# Revit family: Legrand Cabinet XL³ 400 Insulating
name_source: partatom
category: Equipement électrique
units: mm (PartAtom-declared; Revit-internal decimal feet)

## family parameters
Basée sur le plan de construction = Non
Configuration du panneau = Deux colonnes, circuits au sein
Cote de connecteur circulaire = Utiliser le diamètre
Couper avec des vides une fois chargée = Non
Numéro OmniClass = 23.80.30.11.17
Partagée = Non
Point de calcul de pièce = Non
Titre OmniClass = Distribution Boards and Control Panels
Toujours verticalement = Oui
Type d'élément = Tableau de raccordement

## types (5) — shared parameters
Fabricant = Legrand
Finish = Epoxipolyester paint deposited by electrostatic powder
General Conditions of Use = https://export.legrand.com
ICW (until) (kA) = 25
IK with door = 08
IK without door = 07
IN (A) = 400
IP with door = 40
IP without door = 30
IPK (kA) = 52.5
Material = Steel
Material corner = Plastic
Modèle = XL³ 400 Isolant
RAL = 7035
URL = https://www.legrand.fr
depth (mm) = 175 mm  [stored 0.574147 ft]
depth installation zone = 750 mm  [stored 2.46063 ft]
handle Board = Non
handle Cabinet = Oui
width (mm) = 575 mm
width installation zone = 1245 mm
zero-valued in all types: Elévation par défaut

## per-type parameters (varying)
| type | height (mm) | height installation zone |
| 020153-020253 | 600 mm | 600 mm |
| 020154-020254 | 750 mm  [stored 2.46063 ft] | 750 mm  [stored 2.46063 ft] |
| 020155-020255 | 900 mm  [stored 2.95276 ft] | 900 mm  [stored 2.95276 ft] |
| 020156-020256 | 1050 mm | 1050 mm |
| 020157-020257 | 1200 mm | 1200 mm |

note: [stored X ft] marks values corroborated as IEEE doubles in the binary element streams (Revit-internal decimal feet)
